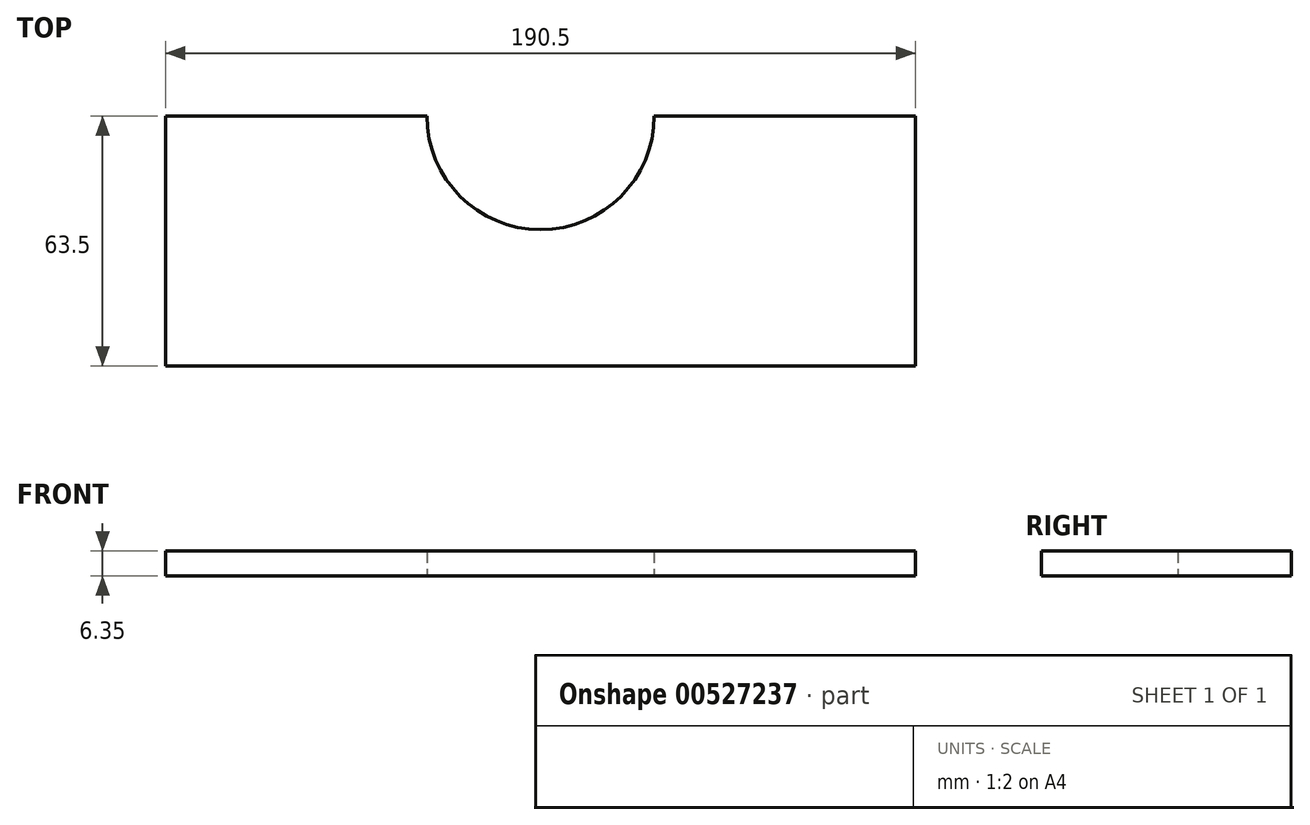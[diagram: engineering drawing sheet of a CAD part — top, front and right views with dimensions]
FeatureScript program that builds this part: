
annotation { "Feature Type Name" : "Feature", "Feature Type Description" : "" }
export const myFeature = defineFeature(function(context is Context, id is Id, definition is map)
    precondition{}
    {
        {
            var Q0;
            Q0=qCreatedBy(makeId("Top.planeOp"),FACE);
            var sketch = newSketch(context, id + "F0", { "sketchPlane" : qUnion([Q0])});
            skLineSegment(sketch, "E0.bottom", {"start": v(0, 0) * mm, "end": v(66.37, 0) * mm});
            skLineSegment(sketch, "E0.top", {"start": v(0, -63.5) * mm, "end": v(190.5, -63.5) * mm});
            skLineSegment(sketch, "E0.left", {"start": v(0, 0) * mm, "end": v(0, -63.5) * mm});
            skLineSegment(sketch, "E0.right", {"start": v(190.5, 0) * mm, "end": v(190.5, -63.5) * mm});
            skArc(sketch, "E1", {"start": v(66.37, 0) * mm, "mid": v(95.25, -28.88) * mm, "end": v(124.13, 0) * mm});
            skLineSegment(sketch, "E2.trimOffspring", {"start": v(124.13, 0) * mm, "end": v(190.5, 0) * mm});
            skSolve(sketch);
        }
        {
            var Q0;
            Q0=makeQuery(id+"F0.imprint","IMPRINT",FACE,{"disambiguationData":[TD([[makeQuery(id+"F0.imprint","IMPRINT",EDGE,{"derivedFrom":sQuery(id+"F0.wireOp",EDGE,"E0.bottom")}),-1.0]])]});
            extrude(context, id + "F1", {"entities" : qUnion([Q0]), "depth" : 6.35 * mm, "offsetDistance" : 25.4 * mm});
        }
    });
